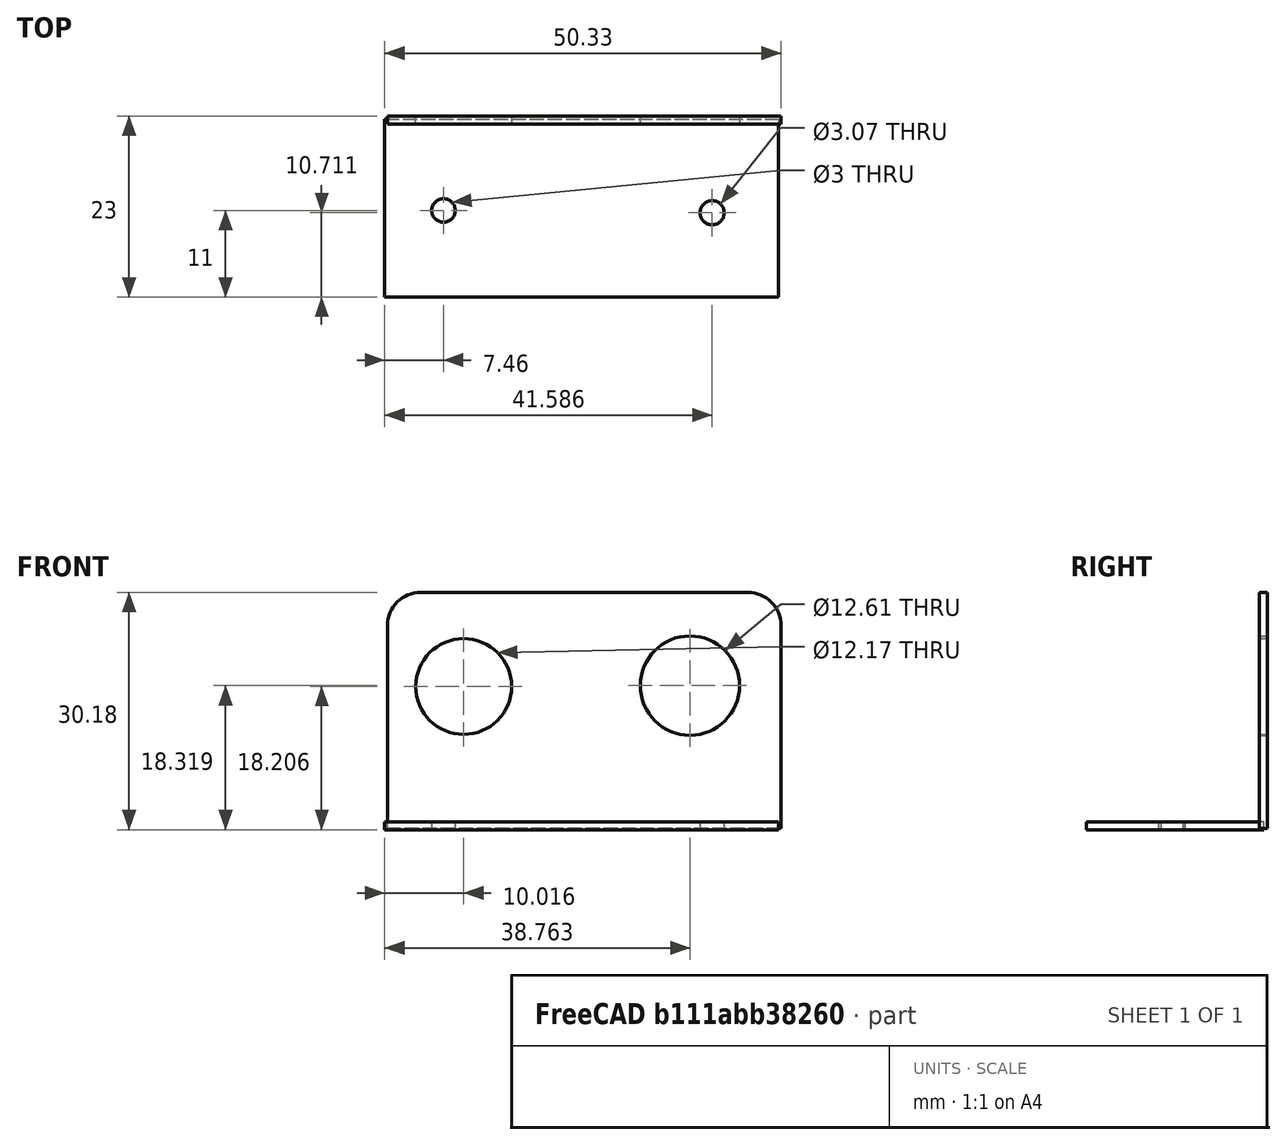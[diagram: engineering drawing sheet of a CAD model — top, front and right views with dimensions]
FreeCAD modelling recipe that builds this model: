
FCSTD DOCUMENT  (FreeCAD 0.19R24291 (Git))
Label: base_ultrasonidos
License: All rights reserved
LicenseURL: http://en.wikipedia.org/wiki/All_rights_reserved
objects: TechDraw::DrawProjGroupItem×3, Sketcher::SketchObject×2, PartDesign::Pad×2, PartDesign::Body×2, App::LinkGroup×1, TechDraw::DrawSVGTemplate×1, TechDraw::DrawProjGroup×1, TechDraw::DrawPage×1
note: 8 computed .brp shape members not serialized (recipe doc carries the construction recipe); baked Part::Feature solids carry a one-line shape summary decoded from their .brp

FEATURE [Sketcher::SketchObject] Sketch
  FullyConstrained = false
  MapMode = 5
  Support = -> [XY_Plane]
  sketch-geometry (6):
    g0: LineSegment StartX=-22.7789 StartY=11.5836 StartZ=0 EndX=27.2211 EndY=11.5836 EndZ=0
    g1: LineSegment StartX=27.2211 StartY=11.5836 StartZ=0 EndX=27.2211 EndY=-10.9971 EndZ=0
    g2: LineSegment StartX=27.2211 StartY=-10.9971 StartZ=0 EndX=-22.7789 EndY=-10.9971 EndZ=0
    g3: LineSegment StartX=-22.7789 StartY=-10.9971 StartZ=0 EndX=-22.7789 EndY=11.5836 EndZ=0
    g4: Circle CenterX=-15.32 CenterY=0 CenterZ=0 NormalX=0 NormalY=0 NormalZ=1 AngleXU=0 Radius=1.49781
    g5: Circle CenterX=18.8064 CenterY=-0.289318 CenterZ=0 NormalX=0 NormalY=0 NormalZ=1 AngleXU=0 Radius=1.53606
  constraints (10):
    c: Coincident(g0,g1)
    c: Coincident(g1,g2)
    c: Coincident(g2,g3)
    c: Coincident(g3,g0)
    c: Horizontal(g0)
    c: Horizontal(g2)
    c: Vertical(g1)
    c: Vertical(g3)
    c: DistanceX(g0,g0) = 50
    c: PointOnObject(g4,g-1)
FEATURE [PartDesign::Pad] Pad
  Direction = (1,1,1)
  Length = 1
  Length2 = 100
  Profile = -> Sketch
  Type = 0
FEATURE [PartDesign::Body] Body  label="base_abajo"
  Group = -> [Sketch,Pad]
  Origin = -> Origin
  Tip = -> Pad
FEATURE [Sketcher::SketchObject] Sketch001
  FullyConstrained = false
  MapMode = 5
  Support = -> [XY_Plane001]
  sketch-geometry (8):
    g0: LineSegment StartX=-97.2101 StartY=28.1823 StartZ=0 EndX=-55.6954 EndY=28.1823 EndZ=0
    g1: LineSegment StartX=-51.4527 StartY=23.9396 StartZ=0 EndX=-51.4527 EndY=-1.81774 EndZ=0
    g2: LineSegment StartX=-51.4527 StartY=-1.81774 StartZ=0 EndX=-101.453 EndY=-1.81774 EndZ=0
    g3: LineSegment StartX=-101.453 StartY=-1.81774 StartZ=0 EndX=-101.453 EndY=23.9396 EndZ=0
    g4: Circle CenterX=-91.7643 CenterY=16.2056 CenterZ=0 NormalX=0 NormalY=0 NormalZ=1 AngleXU=0 Radius=6.0872
    g5: ArcOfCircle CenterX=-97.2101 CenterY=23.9396 CenterZ=0 NormalX=0 NormalY=0 NormalZ=1 AngleXU=0 Radius=4.24264 StartAngle=1.5708 EndAngle=3.14159
    g6: ArcOfCircle CenterX=-55.6954 CenterY=23.9396 CenterZ=0 NormalX=0 NormalY=0 NormalZ=1 AngleXU=0 Radius=4.24264 StartAngle=0 EndAngle=1.5708
    g7: Circle CenterX=-63.0169 CenterY=16.3189 CenterZ=0 NormalX=0 NormalY=0 NormalZ=1 AngleXU=0 Radius=6.30541
  constraints (10):
    c: Coincident(g1,g2)
    c: Coincident(g2,g3)
    c: Horizontal(g0)
    c: Horizontal(g2)
    c: Vertical(g1)
    c: Vertical(g3)
    c: Tangent(g0,g5) = 1.5708
    c: Tangent(g3,g5) = 1.5708
    c: Tangent(g0,g6) = 1.5708
    c: Tangent(g1,g6) = 1.5708
FEATURE [PartDesign::Pad] Pad001
  Direction = (1,1,1)
  Length = 1
  Length2 = 100
  Profile = -> Sketch001
  Type = 0
FEATURE [PartDesign::Body] Body001  label="base_arriba"
  Group = -> [Sketch001,Pad001]
  Origin = -> Origin001
  Placement = pos=(79,12,2) rot=(1,0,0;1.5708rad)
  Tip = -> Pad001
FEATURE [App::LinkGroup] LinkGroup
  ElementList = -> [Body001,Body]
  LinkMode = 0
FEATURE [TechDraw::DrawSVGTemplate] Template
  EditableTexts = Designed_by_Name=Los legendarios; Drawing_number=Drawing number; FC-Date=Date; FC-SC=1:1; FC-SH=Sheet; FC-Title=Base ultrasonidos; Subtitle=Subtitle; Weight=Weight
  Height = 210
  Orientation = 1
  Width = 297
FEATURE [TechDraw::DrawProjGroupItem] ProjItem  label="Front"
  CoarseView = false
  Direction = (0,0,1)
  Focus = 100
  HardHidden = false
  IsoCount = 0
  IsoHidden = false
  IsoVisible = false
  LockPosition = true
  Perspective = false
  Rotation = 0
  RotationVector = (1,0,0)
  ScaleType = 2
  SeamHidden = false
  SeamVisible = true
  SmoothHidden = false
  SmoothVisible = true
  Type = 0
  X = 0
  XDirection = (1,0,0)
  XSource = -> [LinkGroup]
  Y = 0
FEATURE [TechDraw::DrawProjGroupItem] ProjItem001  label="Left"
  CoarseView = false
  Direction = (-1,0,1e-16)
  Focus = 100
  HardHidden = false
  IsoCount = 0
  IsoHidden = false
  IsoVisible = false
  LockPosition = false
  Perspective = false
  Rotation = 0
  RotationVector = (1,0,0)
  ScaleType = 2
  SeamHidden = false
  SeamVisible = true
  SmoothHidden = false
  SmoothVisible = true
  Type = 1
  X = 55.2542
  XDirection = (1e-16,0,1)
  XSource = -> [LinkGroup]
  Y = 0
FEATURE [TechDraw::DrawProjGroupItem] ProjItem002  label="Top"
  CoarseView = false
  Direction = (0,1,0)
  Focus = 100
  HardHidden = false
  IsoCount = 0
  IsoHidden = false
  IsoVisible = false
  LockPosition = false
  Perspective = false
  Rotation = 0
  RotationVector = (1,0,0)
  ScaleType = 2
  SeamHidden = false
  SeamVisible = true
  SmoothHidden = false
  SmoothVisible = true
  Type = 4
  X = 0
  XDirection = (1,0,0)
  XSource = -> [LinkGroup]
  Y = -45.1823
FEATURE [TechDraw::DrawProjGroup] ProjGroup
  Anchor = -> ProjItem
  AutoDistribute = true
  LockPosition = false
  ProjectionType = 0
  Rotation = 0
  ScaleType = 2
  Views = -> [ProjItem,ProjItem001,ProjItem002]
  X = 119.302
  XSource = -> [LinkGroup]
  Y = 147.674
  spacingX = 15
  spacingY = 15
FEATURE [TechDraw::DrawPage] Page
  KeepUpdated = true
  NextBalloonIndex = 1
  ProjectionType = 0
  Template = -> Template
  Views = -> [ProjGroup]
